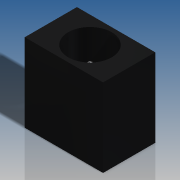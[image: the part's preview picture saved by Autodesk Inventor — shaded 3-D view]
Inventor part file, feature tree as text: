
AUTODESK INVENTOR PART (.ipt)
format: ipt  version: 2016 SP2 (Build 200236200, 236)  size: 188,416 bytes
history: native  units: in
note: dims shown in document units (in); Inventor stores cm internally (conversion verified against a paired STEP export)
features: sketch x3, extrude x2, revolve x1, other x1
ambient origin geometry x8: Origin, YZ Plane, XZ Plane, XY Plane, X Axis, Y Axis, Z Axis, Center Point
bodies: Solid1 (feature_tree), Solid2 (feature_tree)
feature tree (7):
  extrude  "Extrusion1"  Depth=0.2835in
  extrude  "Extrusion2"  TaperAngle=0.0deg  [1 undecoded]
  revolve  "Revolution1"  [1 undecoded]
  sketch  "Sketch2"  dims[d0=0.2835in d1=0.2835in]
  sketch  "Sketch3"  dims[d2=0.189in d3=0.0in]
  sketch  "Sketch4"  dims[d4=0.1575in d5=0.252in d6=0.0in d7=0.0049in d8=0.063in d9=0.0276in d10=0.1969in d11=90.0deg]
  other  "Srf1"
note: 2 required parameter values undecoded (feature->parameter linkage not recoverable at this tier; creation-order binding heuristic only, values carry confidence <= 0.55)